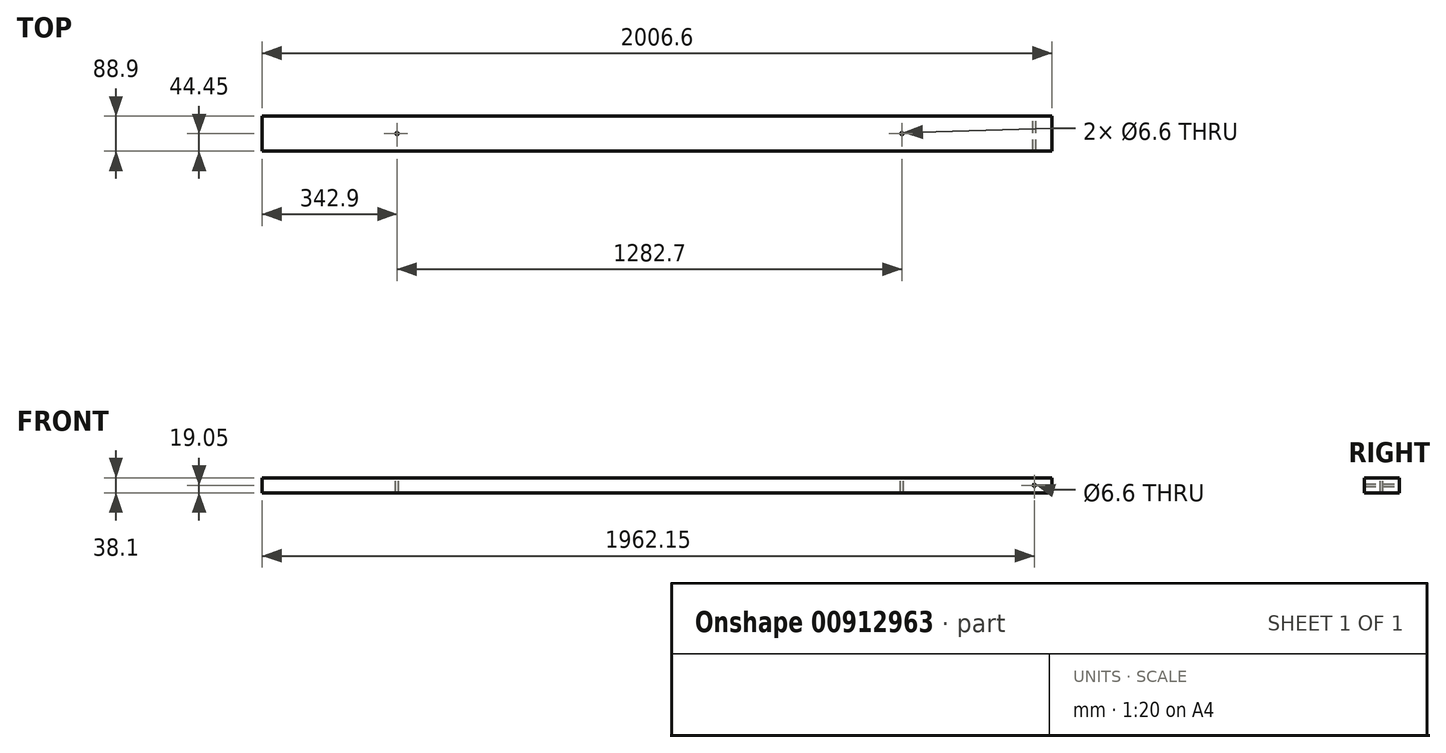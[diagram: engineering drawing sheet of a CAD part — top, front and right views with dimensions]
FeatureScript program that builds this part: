
annotation { "Feature Type Name" : "Feature", "Feature Type Description" : "" }
export const myFeature = defineFeature(function(context is Context, id is Id, definition is map)
    precondition{}
    {
        {
            var Q0;
            Q0=qCreatedBy(makeId("Right.planeOp"),FACE);
            var sketch = newSketch(context, id + "F0", { "sketchPlane" : qUnion([Q0]), "asVersion" : FeatureScriptVersionNumber.V729_UPGRADE_FIXES});
            skLineSegment(sketch, "E0.bottom", {"start": v(44.45, -19.05) * mm, "end": v(-44.45, -19.05) * mm});
            skLineSegment(sketch, "E0.top", {"start": v(44.45, 19.05) * mm, "end": v(-44.45, 19.05) * mm});
            skLineSegment(sketch, "E0.left", {"start": v(44.45, -19.05) * mm, "end": v(44.45, 19.05) * mm});
            skLineSegment(sketch, "E0.right", {"start": v(-44.45, -19.05) * mm, "end": v(-44.45, 19.05) * mm});
            skPoint(sketch, "E0.middle", {"position": v(0, 0) * mm});
            skSolve(sketch);
        }
        {
            var Q0;
            Q0=qSketchRegion(id+"F0",true);
            var Q1;
            Q1=makeQuery(id+"F0.imprint","IMPRINT",FACE,{"disambiguationData":[TD([[makeQuery(id+"F0.imprint","IMPRINT",EDGE,{"derivedFrom":sQuery(id+"F0.wireOp",EDGE,"E0.bottom")}),-1.0]])]});
            extrude(context, id + "F1", {"entities" : qUnion([Q0, Q1]), "depth" : 2006.6 * mm, "offsetDistance" : 25.4 * mm});
        }
        {
            var Q0;
            Q0=makeQuery(id+"F1.opExtrude","SWEPT_FACE",FACE,{"disambiguationData":[OSD([sQuery(id+"F0.wireOp",EDGE,"E0.top")])]});
            var sketch = newSketch(context, id + "F2", { "sketchPlane" : qUnion([Q0])});
            skCircle(sketch, "E1", {"center": v(342.9, 0) * mm, "radius": 3.3 * mm});
            skCircle(sketch, "E2", {"center": v(1625.6, 0) * mm, "radius": 3.3 * mm});
            skLineSegment(sketch, "E3", {"start": v(0, 0) * mm, "end": v(2006.6, 0) * mm, "construction": true});
            skSolve(sketch);
        }
        {
            var Q0;
            Q0 = qSketchRegion(id + "F2", true);
            extrude(context, id + "F3", {"entities" : qUnion([Q0]), "operationType" : NewBodyOperationType.REMOVE, "endBound" : BoundingType.THROUGH_ALL, "oppositeDirection" : true, "depth" : 25.4 * mm, "offsetDistance" : 25.4 * mm});
        }
        {
            var Q0;
            Q0=makeQuery(id+"F1.opExtrude","SWEPT_FACE",FACE,{"disambiguationData":[OSD([sQuery(id+"F0.wireOp",EDGE,"E0.left")])]});
            var sketch = newSketch(context, id + "F4", { "sketchPlane" : qUnion([Q0])});
            skLineSegment(sketch, "E4", {"start": v(-2006.6, -19.05) * mm, "end": v(-1917.7, 19.05) * mm, "construction": true});
            skCircle(sketch, "E5", {"center": v(-1962.15, 0) * mm, "radius": 3.3 * mm});
            skSolve(sketch);
        }
        {
            var Q0;
            Q0 = qSketchRegion(id + "F4", true);
            extrude(context, id + "F5", {"entities" : qUnion([Q0]), "operationType" : NewBodyOperationType.REMOVE, "endBound" : BoundingType.THROUGH_ALL, "oppositeDirection" : true, "depth" : 25.4 * mm, "offsetDistance" : 25.4 * mm});
        }
    });
